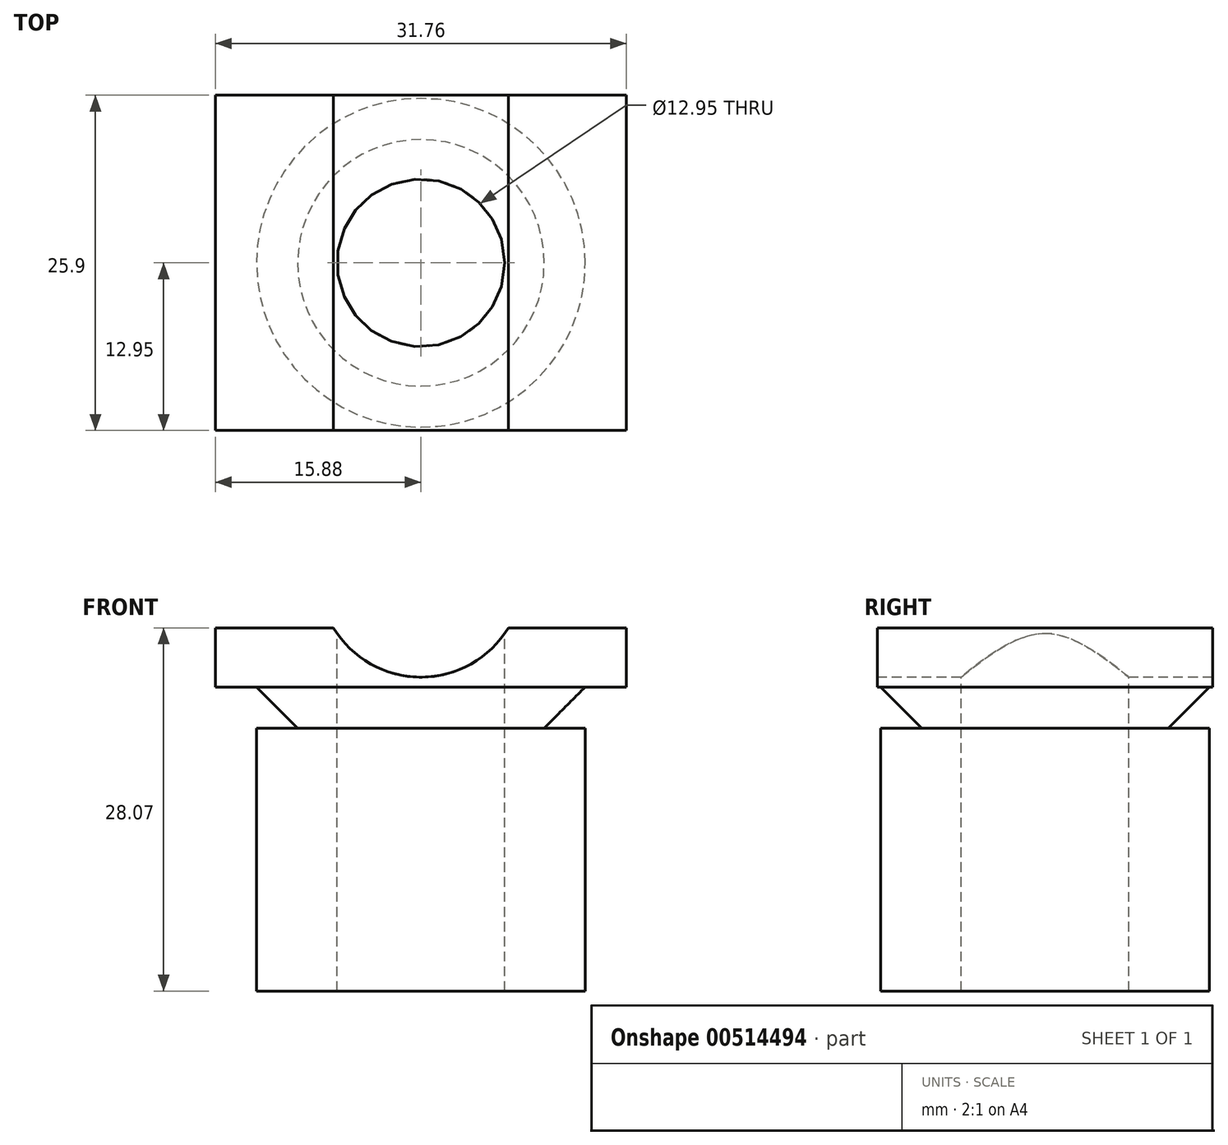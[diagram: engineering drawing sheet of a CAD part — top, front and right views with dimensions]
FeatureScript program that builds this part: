
annotation { "Feature Type Name" : "Feature", "Feature Type Description" : "" }
export const myFeature = defineFeature(function(context is Context, id is Id, definition is map)
    precondition{}
    {
        {
            var Q0;
            Q0=qCreatedBy(makeId("Top.planeOp"),FACE);
            var sketch = newSketch(context, id + "F0", { "sketchPlane" : qUnion([Q0])});
            skCircle(sketch, "E0", {"center": v(0, 0) * mm, "radius": 12.7 * mm});
            skSolve(sketch);
        }
        {
            var Q0;
            Q0=makeQuery(id+"F0.imprint","IMPRINT",FACE,{"disambiguationData":[TD([[makeQuery(id+"F0.imprint","IMPRINT",EDGE,{"derivedFrom":sQuery(id+"F0.wireOp",EDGE,"E0")}),1.0]])]});
            extrude(context, id + "F1", {"entities" : qUnion([Q0]), "depth" : 20.32 * mm, "offsetDistance" : 25.4 * mm, "hasDraft" : true, "draftAngle" : 0 * degree});
        }
        {
            var Q0;
            Q0=makeQuery(id+"F1.opExtrude","CAP_FACE",FACE,{"disambiguationData":[OSD([sQuery(id+"F0.wireOp",EDGE,"E0")])],"isStart":false});
            cPlane(context, id + "F2", {"entities" : qUnion([Q0]), "cplaneType" : CPlaneType.OFFSET, "offset" : 0 * mm, "width" : 152.4 * mm, "height" : 152.4 * mm});
        }
        {
            var Q0;
            Q0=qCreatedBy(id+"F2.planeOp",FACE);
            var sketch = newSketch(context, id + "F3", { "sketchPlane" : qUnion([Q0])});
            skCircle(sketch, "E1", {"center": v(0, 0) * mm, "radius": 9.53 * mm});
            skSolve(sketch);
        }
        {
            var Q0;
            Q0=makeQuery(id+"F3.imprint","IMPRINT",FACE,{"disambiguationData":[TD([[makeQuery(id+"F3.imprint","IMPRINT",EDGE,{"derivedFrom":sQuery(id+"F3.wireOp",EDGE,"E1")}),1.0]])]});
            var Q1;
            Q1=sQuery(id+"F3.wireOp",EDGE,"E1");
            extrude(context, id + "F4", {"entities" : qUnion([Q0]), "operationType" : NewBodyOperationType.ADD, "surfaceEntities" : qUnion([Q1]), "depth" : 3.17 * mm, "offsetDistance" : 25.4 * mm, "hasDraft" : true, "draftAngle" : 45 * degree});
        }
        {
            var Q0;
            Q0=makeQuery(id+"F4.opExtrude","CAP_FACE",FACE,{"disambiguationData":[OSD([sQuery(id+"F3.wireOp",EDGE,"E1")])],"isStart":false});
            cPlane(context, id + "F5", {"entities" : qUnion([Q0]), "cplaneType" : CPlaneType.OFFSET, "offset" : 0 * mm, "width" : 152.4 * mm, "height" : 152.4 * mm});
        }
        {
            var Q0;
            Q0=qCreatedBy(id+"F5.planeOp",FACE);
            var sketch = newSketch(context, id + "F6", { "sketchPlane" : qUnion([Q0])});
            skCircle(sketch, "E2", {"center": v(0, 0) * mm, "radius": 6.48 * mm});
            skSolve(sketch);
        }
        {
            var Q0;
            Q0=makeQuery(id+"F6.imprint","IMPRINT",FACE,{"disambiguationData":[TD([[makeQuery(id+"F6.imprint","IMPRINT",EDGE,{"derivedFrom":sQuery(id+"F6.wireOp",EDGE,"E2")}),1.0]])]});
            var Q1;
            Q1=sQuery(id+"F6.wireOp",EDGE,"E2");
            extrude(context, id + "F7", {"entities" : qUnion([Q0]), "operationType" : NewBodyOperationType.REMOVE, "surfaceEntities" : qUnion([Q1]), "endBound" : BoundingType.THROUGH_ALL, "oppositeDirection" : true, "depth" : 25.4 * mm, "offsetDistance" : 25.4 * mm});
        }
        {
            var Q0;
            Q0=qCreatedBy(id+"F5.planeOp",FACE);
            var sketch = newSketch(context, id + "F8", { "sketchPlane" : qUnion([Q0])});
            skLineSegment(sketch, "E3.bottom", {"start": v(-15.87, -12.95) * mm, "end": v(15.88, -12.95) * mm});
            skLineSegment(sketch, "E3.top", {"start": v(-15.88, 12.95) * mm, "end": v(15.87, 12.95) * mm});
            skLineSegment(sketch, "E3.left", {"start": v(-15.87, -12.95) * mm, "end": v(-15.88, 12.95) * mm});
            skLineSegment(sketch, "E3.right", {"start": v(15.88, -12.95) * mm, "end": v(15.87, 12.95) * mm});
            skPoint(sketch, "E3.middle", {"position": v(0, 0) * mm});
            skSolve(sketch);
        }
        {
            var Q0;
            Q0=makeQuery(id+"F8.imprint","IMPRINT",FACE,{"disambiguationData":[TD([[makeQuery(id+"F8.imprint","IMPRINT",EDGE,{"derivedFrom":sQuery(id+"F8.wireOp",EDGE,"E3.bottom")}),1.0]])]});
            extrude(context, id + "F9", {"entities" : qUnion([Q0]), "operationType" : NewBodyOperationType.ADD, "depth" : 4.57 * mm, "offsetDistance" : 25.4 * mm});
        }
        {
            var Q0;
            Q0=makeQuery(id+"F9.opExtrude","CAP_FACE",FACE,{"disambiguationData":[OSD([sQuery(id+"F8.wireOp",EDGE,"E3.bottom"),sQuery(id+"F8.wireOp",EDGE,"E3.top"),sQuery(id+"F8.wireOp",EDGE,"E3.left"),sQuery(id+"F8.wireOp",EDGE,"E3.right")])],"isStart":false});
            cPlane(context, id + "F10", {"entities" : qUnion([Q0]), "cplaneType" : CPlaneType.OFFSET, "offset" : 0 * mm, "width" : 152.4 * mm, "height" : 152.4 * mm});
        }
        {
            var Q0;
            Q0=qCreatedBy(id+"F10.planeOp",FACE);
            var sketch = newSketch(context, id + "F11", { "sketchPlane" : qUnion([Q0])});
            skCircle(sketch, "E4", {"center": v(0, 0) * mm, "radius": 6.48 * mm});
            skSolve(sketch);
        }
        {
            var Q0;
            Q0=makeQuery(id+"F11.imprint","IMPRINT",FACE,{"disambiguationData":[TD([[makeQuery(id+"F11.imprint","IMPRINT",EDGE,{"derivedFrom":sQuery(id+"F11.wireOp",EDGE,"E4")}),1.0]])]});
            var Q1;
            Q1=sQuery(id+"F11.wireOp",EDGE,"E4");
            extrude(context, id + "F12", {"entities" : qUnion([Q0]), "operationType" : NewBodyOperationType.REMOVE, "surfaceEntities" : qUnion([Q1]), "endBound" : BoundingType.THROUGH_ALL, "oppositeDirection" : true, "depth" : 25.4 * mm, "offsetDistance" : 25.4 * mm});
        }
        {
            var Q0;
            Q0=makeQuery(id+"F9.opExtrude","SWEPT_FACE",FACE,{"disambiguationData":[OSD([sQuery(id+"F8.wireOp",EDGE,"E3.bottom")])]});
            cPlane(context, id + "F13", {"entities" : qUnion([Q0]), "cplaneType" : CPlaneType.OFFSET, "offset" : 0 * mm, "width" : 152.4 * mm, "height" : 152.4 * mm});
        }
        {
            var Q0;
            Q0=qCreatedBy(id+"F13.planeOp",FACE);
            var sketch = newSketch(context, id + "F14", { "sketchPlane" : qUnion([Q0])});
            skCircle(sketch, "E5", {"center": v(0, 32.16) * mm, "radius": 7.9 * mm});
            skSolve(sketch);
        }
        {
            var Q0;
            Q0=makeQuery(id+"F14.imprint","IMPRINT",FACE,{"disambiguationData":[TD([[makeQuery(id+"F14.imprint","IMPRINT",EDGE,{"derivedFrom":sQuery(id+"F14.wireOp",EDGE,"E5")}),1.0]])]});
            var Q1;
            Q1=sQuery(id+"F14.wireOp",EDGE,"E5");
            extrude(context, id + "F15", {"entities" : qUnion([Q0]), "operationType" : NewBodyOperationType.REMOVE, "surfaceEntities" : qUnion([Q1]), "endBound" : BoundingType.THROUGH_ALL, "oppositeDirection" : true, "depth" : 25.4 * mm, "offsetDistance" : 25.4 * mm});
        }
    });
